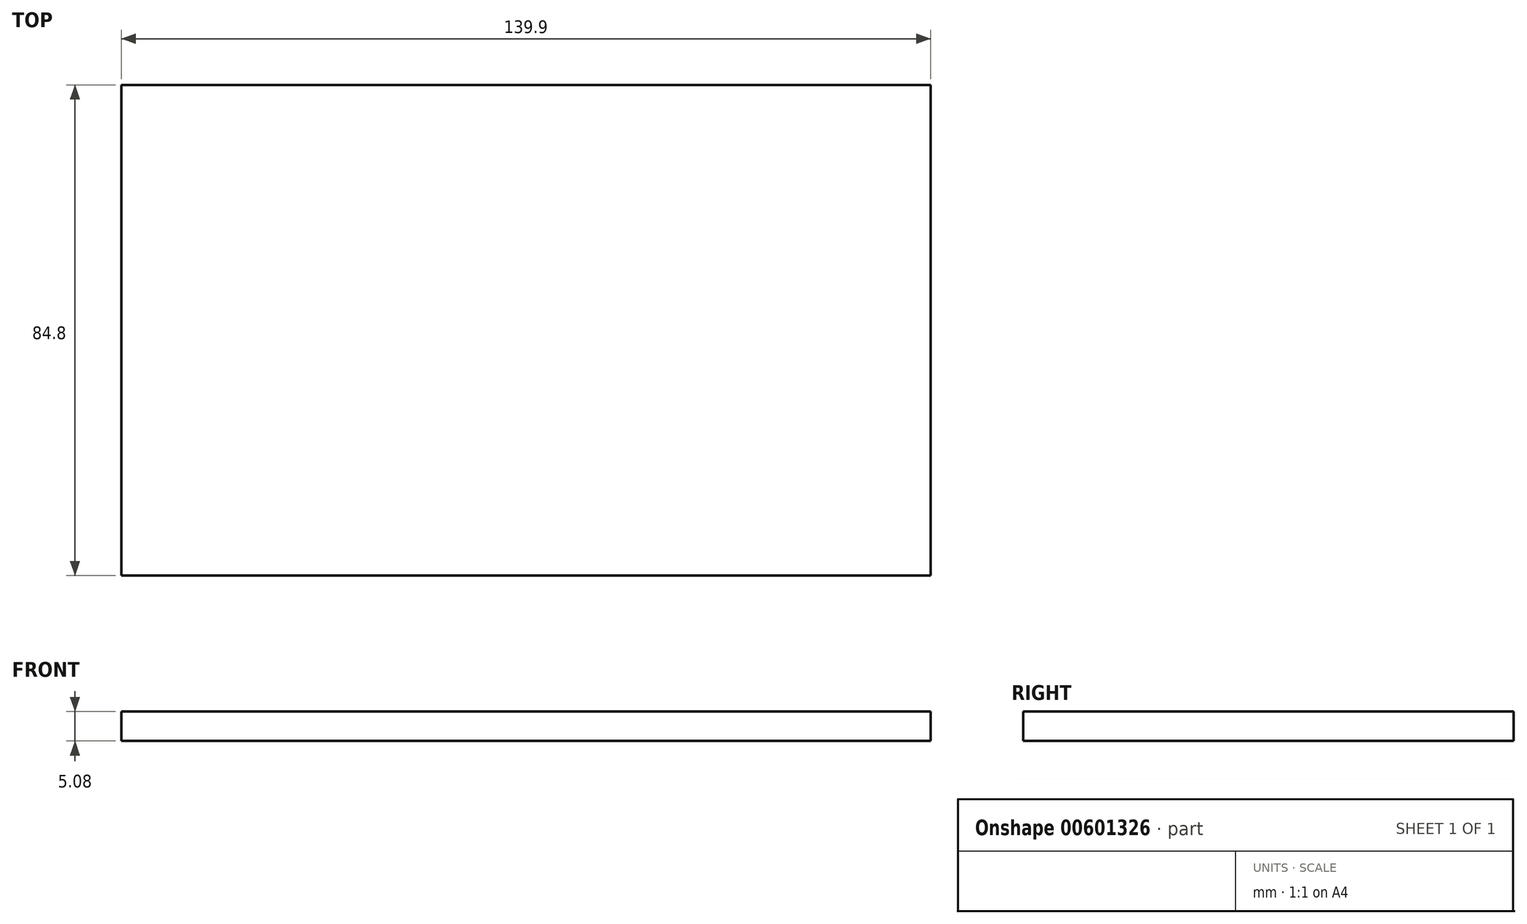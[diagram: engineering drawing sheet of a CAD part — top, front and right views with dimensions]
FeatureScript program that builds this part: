
annotation { "Feature Type Name" : "Feature", "Feature Type Description" : "" }
export const myFeature = defineFeature(function(context is Context, id is Id, definition is map)
    precondition{}
    {
        {
            var Q0;
            Q0=qCreatedBy(makeId("Top.planeOp"),FACE);
            var sketch = newSketch(context, id + "F0", { "sketchPlane" : qUnion([Q0])});
            skLineSegment(sketch, "E0.bottom", {"start": v(-69.35, 52.82) * mm, "end": v(70.55, 52.82) * mm});
            skLineSegment(sketch, "E0.top", {"start": v(-69.35, -31.98) * mm, "end": v(70.55, -31.98) * mm});
            skLineSegment(sketch, "E0.left", {"start": v(-69.35, 52.82) * mm, "end": v(-69.35, -31.98) * mm});
            skLineSegment(sketch, "E0.right", {"start": v(70.55, 52.82) * mm, "end": v(70.55, -31.98) * mm});
            skSolve(sketch);
        }
        {
            var Q0;
            Q0=makeQuery(id+"F0.imprint","IMPRINT",FACE,{"disambiguationData":[TD([[makeQuery(id+"F0.imprint","IMPRINT",EDGE,{"derivedFrom":sQuery(id+"F0.wireOp",EDGE,"E0.bottom")}),-1.0]])]});
            extrude(context, id + "F1", {"entities" : qUnion([Q0]), "oppositeDirection" : true, "depth" : 5.08 * mm, "offsetDistance" : 25.4 * mm});
        }
    });
